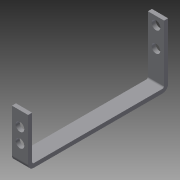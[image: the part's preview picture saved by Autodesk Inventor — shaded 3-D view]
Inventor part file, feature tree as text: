
AUTODESK INVENTOR PART (.ipt)
format: ipt  version: 2013 (Build 170138000, 138)  size: 208,384 bytes
history: native  units: in
note: dims shown in document units (in); Inventor stores cm internally (conversion verified against a paired STEP export)
features: other x8, sheet_metal_op x7, sketch x6, reference x2
ambient origin geometry x8: Origin, YZ Plane, XZ Plane, XY Plane, X Axis, Y Axis, Z Axis, Center Point
bodies: Solid1 (feature_tree)
feature tree (23):
  sheet_metal_op  "Face1"
  sheet_metal_op  "Flange1"
  sheet_metal_op  "Flange2"
  sketch  "Sketch1"  dims[d0=0.5in]
  other  "Plate1"
  sketch  "Sketch2"  dims[d1=1.75in]
  other  "Plate2"
  sheet_metal_op  "Bend1"
  sheet_metal_op  "Corner1"
  sketch  "Sketch3"  dims[d2=0.125in]
  reference  "Reference1"
  reference  "Reference2"
  sketch  "Sketch5"  dims[d4=0.0625in]
  other  "Plate3"
  sheet_metal_op  "Bend2"
  sheet_metal_op  "Corner2"
  sketch  "Sketch6"  dims[d5=0.25in d6=0.125in d7=4.1472in d8=90.0deg d9=0.05in d10=0.5in d11=0.125in d12=0.125in d13=0.125in d14=0.0in d19=0.125in d20=0.0625in d21=0.25in d22=0.125in d23=1.5in d24=90.0deg d25=0.05in d26=0.5in d27=0.125in d28=0.125in d29=0.4417in d31=0.442in d32=0.266in d33=0.266in d34=0.125in d35=0.0in d15=0.0625in d16=0.125in d17=0.0in d18=0.125in]
  other  "Cut1"
  other  "Cut3"
  other  "Definition1"
  sketch  "Sketch4"  dims[d3=0.125in]
  other  "Cut2"
  other  "Cut4"
